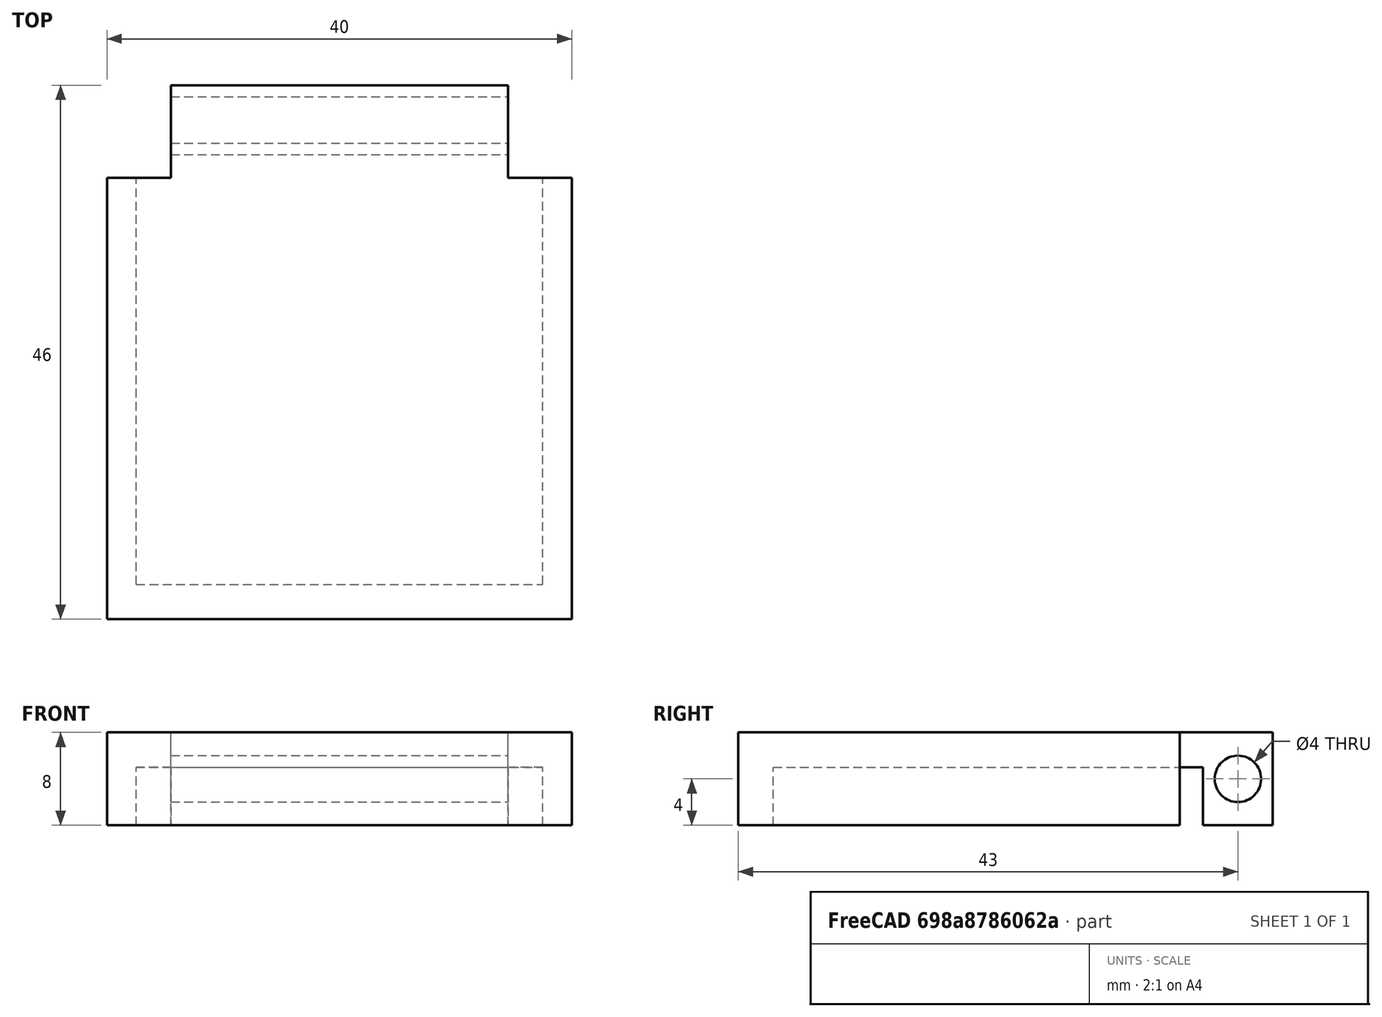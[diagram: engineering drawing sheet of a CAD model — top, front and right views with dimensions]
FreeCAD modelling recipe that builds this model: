
FCSTD DOCUMENT  (FreeCAD 0.18RUnknown)
Label: vim
License: All rights reserved
LicenseURL: http://en.wikipedia.org/wiki/All_rights_reserved
objects: Part::Box×4, Part::Cut×4, Part::Cylinder×1
note: 9 computed .brp shape members not serialized (recipe doc carries the construction recipe); baked Part::Feature solids carry a one-line shape summary decoded from their .brp

FEATURE [Part::Box] Box  label="mainbody"
  AttacherType = Attacher::AttachEngine3D
  Height = 8
  Length = 40
  Placement = pos=(0,0,26) rot=(0,0,1;0rad)
  Width = 46
FEATURE [Part::Box] Box001  label="hingeplate1"
  AttacherType = Attacher::AttachEngine3D
  Height = 8
  Length = 5.5
  Placement = pos=(0,38,26) rot=(0,0,1;0rad)
  Width = 8
FEATURE [Part::Box] Box002  label="hingeplate2"
  AttacherType = Attacher::AttachEngine3D
  Height = 8
  Length = 5.5
  Placement = pos=(34.5,38,26) rot=(0,0,1;0rad)
  Width = 8
FEATURE [Part::Cylinder] Cylinder003  label="axel"
  Angle = 360
  AttacherType = Attacher::AttachEngine3D
  Height = 45
  Placement = pos=(-2,43,30) rot=(0,1,0;1.5708rad)
  Radius = 2
FEATURE [Part::Box] Box003  label="mainbody001"
  AttacherType = Attacher::AttachEngine3D
  Height = 5
  Length = 35
  Placement = pos=(2.5,3,26) rot=(0,0,1;0rad)
  Width = 37
FEATURE [Part::Cut] Cut
  Base = -> Box
  Tool = -> Box003
FEATURE [Part::Cut] Cut001
  Base = -> Cut
  Tool = -> Box001
FEATURE [Part::Cut] Cut002
  Base = -> Cut001
  Tool = -> Box002
FEATURE [Part::Cut] Cut003
  Base = -> Cut002
  Tool = -> Cylinder003
